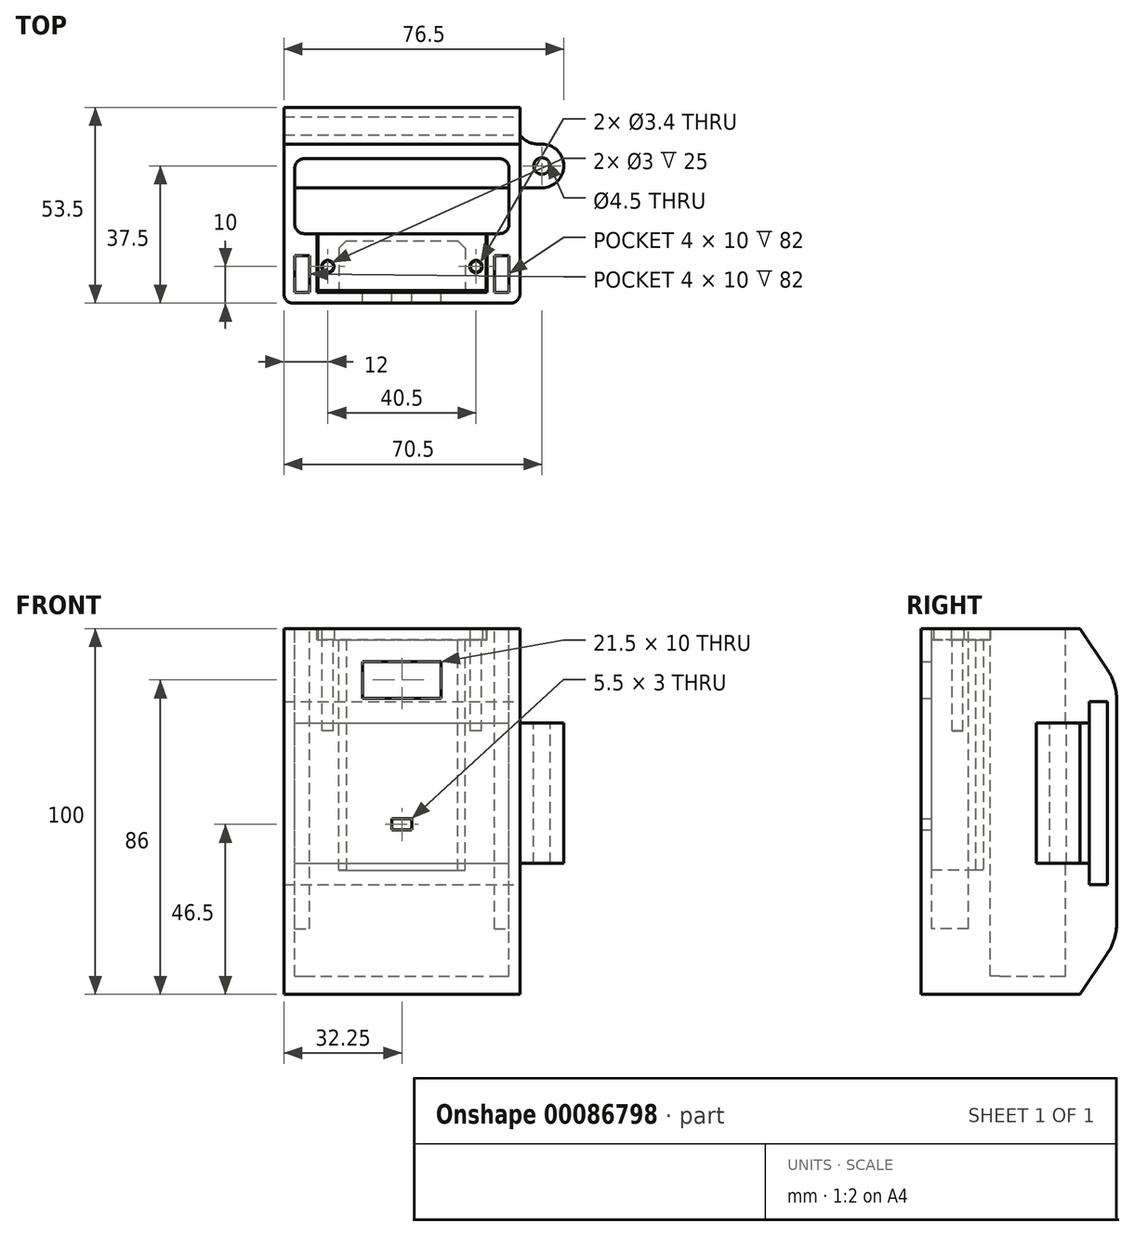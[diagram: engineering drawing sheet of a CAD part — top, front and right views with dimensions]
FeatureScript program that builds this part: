
annotation { "Feature Type Name" : "Feature", "Feature Type Description" : "" }
export const myFeature = defineFeature(function(context is Context, id is Id, definition is map)
    precondition{}
    {
        {
            var Q0;
            Q0=qCreatedBy(makeId("Top.planeOp"),FACE);
            var sketch = newSketch(context, id + "F0", { "sketchPlane" : qUnion([Q0])});
            skLineSegment(sketch, "E0.top", {"start": v(0, 43.5) * mm, "end": v(64.5, 43.5) * mm});
            skLineSegment(sketch, "E0.left", {"start": v(0, 0) * mm, "end": v(0, 43.5) * mm});
            skLineSegment(sketch, "E0.right", {"start": v(64.5, 0) * mm, "end": v(64.5, 43.5) * mm});
            skLineSegment(sketch, "E1.bottom", {"start": v(3, 19) * mm, "end": v(61.5, 19) * mm});
            skLineSegment(sketch, "E1.top", {"start": v(3, 39.5) * mm, "end": v(61.5, 39.5) * mm});
            skLineSegment(sketch, "E1.left", {"start": v(3, 19) * mm, "end": v(3, 39.5) * mm});
            skLineSegment(sketch, "E1.right", {"start": v(61.5, 19) * mm, "end": v(61.5, 39.5) * mm});
            skLineSegment(sketch, "E2.bottom", {"start": v(57.5, 13) * mm, "end": v(61.5, 13) * mm});
            skLineSegment(sketch, "E2.top", {"start": v(57.5, 3) * mm, "end": v(61.5, 3) * mm});
            skLineSegment(sketch, "E2.left", {"start": v(57.5, 13) * mm, "end": v(57.5, 3) * mm});
            skLineSegment(sketch, "E2.right", {"start": v(61.5, 13) * mm, "end": v(61.5, 3) * mm});
            skLineSegment(sketch, "E3", {"start": v(64.5, 43.5) * mm, "end": v(70.5, 43.5) * mm});
            skArc(sketch, "E4", {"start": v(70.5, 31.5) * mm, "mid": v(76.5, 37.5) * mm, "end": v(70.5, 43.5) * mm});
            skLineSegment(sketch, "E5", {"start": v(70.5, 31.5) * mm, "end": v(64.5, 31.5) * mm});
            skLineSegment(sketch, "E6", {"start": v(70.5, 37.5) * mm, "end": v(76.5, 37.5) * mm, "construction": true});
            skCircle(sketch, "E7", {"center": v(70.5, 37.5) * mm, "radius": 2.25 * mm});
            skCircle(sketch, "E8", {"center": v(70.5, 37.5) * mm, "radius": 3.75 * mm});
            skLineSegment(sketch, "E9.bottom", {"start": v(3, 13) * mm, "end": v(7, 13) * mm});
            skLineSegment(sketch, "E9.top", {"start": v(3, 3) * mm, "end": v(7, 3) * mm});
            skLineSegment(sketch, "E9.left", {"start": v(3, 13) * mm, "end": v(3, 3) * mm});
            skLineSegment(sketch, "E9.right", {"start": v(7, 13) * mm, "end": v(7, 3) * mm});
            skLineSegment(sketch, "E10", {"start": v(0, 31.5) * mm, "end": v(-6, 31.5) * mm});
            skArc(sketch, "E11", {"start": v(-6, 43.5) * mm, "mid": v(-12, 37.5) * mm, "end": v(-6, 31.5) * mm});
            skLineSegment(sketch, "E12", {"start": v(-6, 43.5) * mm, "end": v(0, 43.5) * mm});
            skLineSegment(sketch, "E13", {"start": v(-6, 37.5) * mm, "end": v(-12, 37.5) * mm, "construction": true});
            skCircle(sketch, "E14", {"center": v(-6, 37.5) * mm, "radius": 2.25 * mm});
            skCircle(sketch, "E15", {"center": v(-6, 37.5) * mm, "radius": 3.75 * mm});
            skLineSegment(sketch, "E16", {"start": v(64.5, 0) * mm, "end": v(0, 0) * mm});
            skLineSegment(sketch, "E17.bottom", {"start": v(15, 17) * mm, "end": v(49.5, 17) * mm});
            skLineSegment(sketch, "E17.top", {"start": v(15, 3) * mm, "end": v(49.5, 3) * mm});
            skLineSegment(sketch, "E17.left", {"start": v(15, 17) * mm, "end": v(15, 3) * mm});
            skLineSegment(sketch, "E17.right", {"start": v(49.5, 17) * mm, "end": v(49.5, 3) * mm});
            skLineSegment(sketch, "E18", {"start": v(15, 10) * mm, "end": v(0, 10) * mm, "construction": true});
            skLineSegment(sketch, "E19", {"start": v(49.5, 10) * mm, "end": v(64.5, 10) * mm, "construction": true});
            skLineSegment(sketch, "E20", {"start": v(9, 19) * mm, "end": v(9, 3) * mm});
            skLineSegment(sketch, "E21", {"start": v(9, 3) * mm, "end": v(15, 3) * mm});
            skLineSegment(sketch, "E22", {"start": v(49.5, 3) * mm, "end": v(55.5, 3) * mm});
            skLineSegment(sketch, "E23", {"start": v(55.5, 3) * mm, "end": v(55.5, 19) * mm});
            skLineSegment(sketch, "E24", {"start": v(9, 10) * mm, "end": v(15, 10) * mm, "construction": true});
            skLineSegment(sketch, "E25", {"start": v(49.5, 10) * mm, "end": v(55.5, 10) * mm, "construction": true});
            skCircle(sketch, "E26", {"center": v(52.5, 10) * mm, "radius": 1.5 * mm});
            skCircle(sketch, "E27", {"center": v(12, 10) * mm, "radius": 1.5 * mm});
            skSolve(sketch);
        }
        {
            var Q0;
            {var subQ7=sQuery(id+"F0.wireOp",EDGE,"E0.top");Q0=makeQuery(id+"F0.imprint","IMPRINT",FACE,{"disambiguationData":[TD([[makeQuery(id+"F0.imprint","IMPRINT",EDGE,{"derivedFrom":subQ7}),-1.0]])]});}
            extrude(context, id + "F1", {"entities" : qUnion([Q0]), "oppositeDirection" : true, "depth" : 100 * mm});
        }
        {
            var Q0;
            Q0=makeQuery(id+"F0.imprint","IMPRINT",FACE,{"disambiguationData":[TD([[makeQuery(id+"F0.imprint","IMPRINT",EDGE,{"derivedFrom":sQuery(id+"F0.wireOp",EDGE,"E17.bottom")}),1.0]])]});
            var Q1;
            Q1=makeQuery(id+"F1.opExtrude","CAP_FACE",FACE,{"disambiguationData":[OSD([sQuery(id+"F0.wireOp",EDGE,"E0.top"),sQuery(id+"F0.wireOp",EDGE,"E0.left"),sQuery(id+"F0.wireOp",EDGE,"E0.right"),sQuery(id+"F0.wireOp",EDGE,"E1.bottom"),sQuery(id+"F0.wireOp",EDGE,"E1.top"),sQuery(id+"F0.wireOp",EDGE,"E1.left"),sQuery(id+"F0.wireOp",EDGE,"E1.right"),sQuery(id+"F0.wireOp",EDGE,"E2.bottom"),sQuery(id+"F0.wireOp",EDGE,"E2.top"),sQuery(id+"F0.wireOp",EDGE,"E2.left"),sQuery(id+"F0.wireOp",EDGE,"E2.right"),sQuery(id+"F0.wireOp",EDGE,"E9.bottom"),sQuery(id+"F0.wireOp",EDGE,"E9.top"),sQuery(id+"F0.wireOp",EDGE,"E9.left"),sQuery(id+"F0.wireOp",EDGE,"E9.right"),sQuery(id+"F0.wireOp",EDGE,"E16"),sQuery(id+"F0.wireOp",EDGE,"E17.top"),sQuery(id+"F0.wireOp",EDGE,"E20"),sQuery(id+"F0.wireOp",EDGE,"E21"),sQuery(id+"F0.wireOp",EDGE,"E22"),sQuery(id+"F0.wireOp",EDGE,"E23")])],"isStart":false});
            extrude(context, id + "F2", {"entities" : qUnion([Q0]), "operationType" : NewBodyOperationType.ADD, "endBound" : BoundingType.UP_TO_SURFACE, "oppositeDirection" : true, "endBoundEntityFace" : qUnion([Q1]), "depth" : 25 * mm, "hasSecondDirection" : true, "secondDirectionOppositeDirection" : true, "secondDirectionDepth" : 3 * mm});
        }
        {
            var Q0;
            Q0=makeQuery(id+"F0.imprint","IMPRINT",FACE,{"disambiguationData":[TD([[makeQuery(id+"F0.imprint","IMPRINT",EDGE,{"derivedFrom":sQuery(id+"F0.wireOp",EDGE,"E26")}),1.0]])]});
            var Q1;
            Q1=makeQuery(id+"F0.imprint","IMPRINT",FACE,{"disambiguationData":[TD([[makeQuery(id+"F0.imprint","IMPRINT",EDGE,{"derivedFrom":sQuery(id+"F0.wireOp",EDGE,"E27")}),1.0]])]});
            var Q2;
            {var subQ0=sQuery(id+"F0.wireOp",EDGE,"E23");var subQ1=sQuery(id+"F0.wireOp",EDGE,"E22");var subQ2=sQuery(id+"F0.wireOp",EDGE,"E21");var subQ3=sQuery(id+"F0.wireOp",EDGE,"E20");var subQ4=sQuery(id+"F0.wireOp",EDGE,"E17.top");var subQ5=sQuery(id+"F0.wireOp",EDGE,"E16");var subQ6=sQuery(id+"F0.wireOp",EDGE,"E9.right");var subQ7=sQuery(id+"F0.wireOp",EDGE,"E9.left");var subQ8=sQuery(id+"F0.wireOp",EDGE,"E9.top");var subQ9=sQuery(id+"F0.wireOp",EDGE,"E9.bottom");var subQ10=sQuery(id+"F0.wireOp",EDGE,"E2.right");var subQ11=sQuery(id+"F0.wireOp",EDGE,"E2.left");var subQ12=sQuery(id+"F0.wireOp",EDGE,"E2.top");var subQ13=sQuery(id+"F0.wireOp",EDGE,"E2.bottom");var subQ14=sQuery(id+"F0.wireOp",EDGE,"E1.right");var subQ15=sQuery(id+"F0.wireOp",EDGE,"E1.left");var subQ16=sQuery(id+"F0.wireOp",EDGE,"E1.top");var subQ17=sQuery(id+"F0.wireOp",EDGE,"E1.bottom");var subQ18=sQuery(id+"F0.wireOp",EDGE,"E0.right");var subQ19=sQuery(id+"F0.wireOp",EDGE,"E0.left");var subQ20=sQuery(id+"F0.wireOp",EDGE,"E0.top");Q2=makeQuery(id+"F2.boolean.opBoolean","MERGE",FACE,{"derivedFrom":[makeQuery(id+"F1.opExtrude","CAP_FACE",FACE,{"disambiguationData":[OSD([subQ20,subQ19,subQ18,subQ17,subQ16,subQ15,subQ14,subQ13,subQ12,subQ11,subQ10,subQ9,subQ8,subQ7,subQ6,subQ5,subQ4,subQ3,subQ2,subQ1,subQ0])],"isStart":false}),makeQuery(id+"F2.opExtrude","CAP_FACE",FACE,{"disambiguationData":[OSD([subQ20,subQ19,subQ18,subQ17,subQ16,subQ15,subQ14,subQ13,subQ12,subQ11,subQ10,subQ9,subQ8,subQ7,subQ6,subQ5,subQ4,subQ3,subQ2,subQ1,subQ0])],"isStart":false})]});}
            extrude(context, id + "F3", {"entities" : qUnion([Q0, Q1]), "operationType" : NewBodyOperationType.ADD, "endBound" : BoundingType.UP_TO_SURFACE, "oppositeDirection" : true, "endBoundEntityFace" : qUnion([Q2]), "depth" : 25 * mm, "hasSecondDirection" : true, "secondDirectionOppositeDirection" : true, "secondDirectionDepth" : 28 * mm});
        }
        {
            var Q0;
            Q0=makeQuery(id+"F0.imprint","IMPRINT",FACE,{"disambiguationData":[TD([[makeQuery(id+"F0.imprint","IMPRINT",EDGE,{"derivedFrom":sQuery(id+"F0.wireOp",EDGE,"E1.top")}),-1.0]])]});
            var Q1;
            {var subQ0=sQuery(id+"F0.wireOp",EDGE,"E23");var subQ1=sQuery(id+"F0.wireOp",EDGE,"E22");var subQ2=sQuery(id+"F0.wireOp",EDGE,"E21");var subQ3=sQuery(id+"F0.wireOp",EDGE,"E20");var subQ4=sQuery(id+"F0.wireOp",EDGE,"E17.top");var subQ5=sQuery(id+"F0.wireOp",EDGE,"E16");var subQ6=sQuery(id+"F0.wireOp",EDGE,"E9.right");var subQ7=sQuery(id+"F0.wireOp",EDGE,"E9.left");var subQ8=sQuery(id+"F0.wireOp",EDGE,"E9.top");var subQ9=sQuery(id+"F0.wireOp",EDGE,"E9.bottom");var subQ10=sQuery(id+"F0.wireOp",EDGE,"E2.right");var subQ11=sQuery(id+"F0.wireOp",EDGE,"E2.left");var subQ12=sQuery(id+"F0.wireOp",EDGE,"E2.top");var subQ13=sQuery(id+"F0.wireOp",EDGE,"E2.bottom");var subQ14=sQuery(id+"F0.wireOp",EDGE,"E1.right");var subQ15=sQuery(id+"F0.wireOp",EDGE,"E1.left");var subQ16=sQuery(id+"F0.wireOp",EDGE,"E1.top");var subQ17=sQuery(id+"F0.wireOp",EDGE,"E1.bottom");var subQ18=sQuery(id+"F0.wireOp",EDGE,"E0.right");var subQ19=sQuery(id+"F0.wireOp",EDGE,"E0.left");var subQ20=sQuery(id+"F0.wireOp",EDGE,"E0.top");Q1=makeQuery(id+"F3.boolean.opBoolean","MERGE",FACE,{"derivedFrom":[makeQuery(id+"F2.boolean.opBoolean","MERGE",FACE,{"derivedFrom":[makeQuery(id+"F1.opExtrude","CAP_FACE",FACE,{"disambiguationData":[OSD([subQ20,subQ19,subQ18,subQ17,subQ16,subQ15,subQ14,subQ13,subQ12,subQ11,subQ10,subQ9,subQ8,subQ7,subQ6,subQ5,subQ4,subQ3,subQ2,subQ1,subQ0])],"isStart":false}),makeQuery(id+"F2.opExtrude","CAP_FACE",FACE,{"disambiguationData":[OSD([subQ20,subQ19,subQ18,subQ17,subQ16,subQ15,subQ14,subQ13,subQ12,subQ11,subQ10,subQ9,subQ8,subQ7,subQ6,subQ5,subQ4,subQ3,subQ2,subQ1,subQ0])],"isStart":false})]}),makeQuery(id+"F3.opExtrude","CAP_FACE",FACE,{"disambiguationData":[OSD([subQ20,subQ19,subQ18,subQ17,subQ16,subQ15,subQ14,subQ13,subQ12,subQ11,subQ10,subQ9,subQ8,subQ7,subQ6,subQ5,subQ4,subQ3,subQ2,subQ1,subQ0]),ownerDisambiguation([makeQuery(id+"F3.opExtrude","SWEPT_BODY",BODY,{"disambiguationData":[OSD([sQuery(id+"F0.wireOp",EDGE,"E26")])]})])],"isStart":false}),makeQuery(id+"F3.opExtrude","CAP_FACE",FACE,{"disambiguationData":[OSD([subQ20,subQ19,subQ18,subQ17,subQ16,subQ15,subQ14,subQ13,subQ12,subQ11,subQ10,subQ9,subQ8,subQ7,subQ6,subQ5,subQ4,subQ3,subQ2,subQ1,subQ0]),ownerDisambiguation([makeQuery(id+"F3.opExtrude","SWEPT_BODY",BODY,{"disambiguationData":[OSD([sQuery(id+"F0.wireOp",EDGE,"E27")])]})])],"isStart":false})]});}
            extrude(context, id + "F4", {"entities" : qUnion([Q0]), "operationType" : NewBodyOperationType.ADD, "endBound" : BoundingType.UP_TO_SURFACE, "oppositeDirection" : true, "endBoundEntityFace" : qUnion([Q1]), "depth" : 25 * mm, "hasSecondDirection" : true, "secondDirectionOppositeDirection" : true, "secondDirectionDepth" : 95 * mm});
        }
        {
            var Q0;
            Q0=makeQuery(id+"F0.imprint","IMPRINT",FACE,{"disambiguationData":[TD([[makeQuery(id+"F0.imprint","IMPRINT",EDGE,{"derivedFrom":sQuery(id+"F0.wireOp",EDGE,"E17.bottom")}),-1.0]])]});
            var Q1;
            {var subQ0=sQuery(id+"F0.wireOp",EDGE,"E23");var subQ1=sQuery(id+"F0.wireOp",EDGE,"E22");var subQ2=sQuery(id+"F0.wireOp",EDGE,"E21");var subQ3=sQuery(id+"F0.wireOp",EDGE,"E20");var subQ4=sQuery(id+"F0.wireOp",EDGE,"E17.top");var subQ5=sQuery(id+"F0.wireOp",EDGE,"E16");var subQ6=sQuery(id+"F0.wireOp",EDGE,"E9.right");var subQ7=sQuery(id+"F0.wireOp",EDGE,"E9.left");var subQ8=sQuery(id+"F0.wireOp",EDGE,"E9.top");var subQ9=sQuery(id+"F0.wireOp",EDGE,"E9.bottom");var subQ10=sQuery(id+"F0.wireOp",EDGE,"E2.right");var subQ11=sQuery(id+"F0.wireOp",EDGE,"E2.left");var subQ12=sQuery(id+"F0.wireOp",EDGE,"E2.top");var subQ13=sQuery(id+"F0.wireOp",EDGE,"E2.bottom");var subQ14=sQuery(id+"F0.wireOp",EDGE,"E1.right");var subQ15=sQuery(id+"F0.wireOp",EDGE,"E1.left");var subQ16=sQuery(id+"F0.wireOp",EDGE,"E1.top");var subQ17=sQuery(id+"F0.wireOp",EDGE,"E1.bottom");var subQ18=sQuery(id+"F0.wireOp",EDGE,"E0.right");var subQ19=sQuery(id+"F0.wireOp",EDGE,"E0.left");var subQ20=sQuery(id+"F0.wireOp",EDGE,"E0.top");Q1=makeQuery(id+"F4.boolean.opBoolean","MERGE",FACE,{"derivedFrom":[makeQuery(id+"F3.boolean.opBoolean","MERGE",FACE,{"derivedFrom":[makeQuery(id+"F2.boolean.opBoolean","MERGE",FACE,{"derivedFrom":[makeQuery(id+"F1.opExtrude","CAP_FACE",FACE,{"disambiguationData":[OSD([subQ20,subQ19,subQ18,subQ17,subQ16,subQ15,subQ14,subQ13,subQ12,subQ11,subQ10,subQ9,subQ8,subQ7,subQ6,subQ5,subQ4,subQ3,subQ2,subQ1,subQ0])],"isStart":false}),makeQuery(id+"F2.opExtrude","CAP_FACE",FACE,{"disambiguationData":[OSD([subQ20,subQ19,subQ18,subQ17,subQ16,subQ15,subQ14,subQ13,subQ12,subQ11,subQ10,subQ9,subQ8,subQ7,subQ6,subQ5,subQ4,subQ3,subQ2,subQ1,subQ0])],"isStart":false})]}),makeQuery(id+"F3.opExtrude","CAP_FACE",FACE,{"disambiguationData":[OSD([subQ20,subQ19,subQ18,subQ17,subQ16,subQ15,subQ14,subQ13,subQ12,subQ11,subQ10,subQ9,subQ8,subQ7,subQ6,subQ5,subQ4,subQ3,subQ2,subQ1,subQ0]),ownerDisambiguation([makeQuery(id+"F3.opExtrude","SWEPT_BODY",BODY,{"disambiguationData":[OSD([sQuery(id+"F0.wireOp",EDGE,"E26")])]})])],"isStart":false}),makeQuery(id+"F3.opExtrude","CAP_FACE",FACE,{"disambiguationData":[OSD([subQ20,subQ19,subQ18,subQ17,subQ16,subQ15,subQ14,subQ13,subQ12,subQ11,subQ10,subQ9,subQ8,subQ7,subQ6,subQ5,subQ4,subQ3,subQ2,subQ1,subQ0]),ownerDisambiguation([makeQuery(id+"F3.opExtrude","SWEPT_BODY",BODY,{"disambiguationData":[OSD([sQuery(id+"F0.wireOp",EDGE,"E27")])]})])],"isStart":false})]}),makeQuery(id+"F4.opExtrude","CAP_FACE",FACE,{"disambiguationData":[OSD([subQ20,subQ19,subQ18,subQ17,subQ16,subQ15,subQ14,subQ13,subQ12,subQ11,subQ10,subQ9,subQ8,subQ7,subQ6,subQ5,subQ4,subQ3,subQ2,subQ1,subQ0])],"isStart":false})]});}
            extrude(context, id + "F5", {"entities" : qUnion([Q0]), "operationType" : NewBodyOperationType.ADD, "endBound" : BoundingType.UP_TO_SURFACE, "oppositeDirection" : true, "endBoundEntityFace" : qUnion([Q1]), "depth" : 25 * mm, "hasSecondDirection" : true, "secondDirectionOppositeDirection" : true, "secondDirectionDepth" : 66 * mm});
        }
        {
            var Q0;
            {var subQ1=sQuery(id+"F0.wireOp",EDGE,"E3");Q0=makeQuery(id+"F0.imprint","IMPRINT",FACE,{"disambiguationData":[TD([[makeQuery(id+"F0.imprint","IMPRINT",EDGE,{"derivedFrom":subQ1}),-1.0]])]});}
            var Q1;
            Q1=makeQuery(id+"F0.imprint","IMPRINT",FACE,{"disambiguationData":[TD([[makeQuery(id+"F0.imprint","IMPRINT",EDGE,{"derivedFrom":sQuery(id+"F0.wireOp",EDGE,"E7")}),-1.0]])]});
            extrude(context, id + "F6", {"entities" : qUnion([Q0, Q1]), "operationType" : NewBodyOperationType.ADD, "oppositeDirection" : true, "depth" : 64.2 * mm, "hasSecondDirection" : true, "secondDirectionOppositeDirection" : true, "secondDirectionDepth" : 25.8 * mm});
        }
        {
            var Q0;
            Q0=makeQuery(id+"F0.imprint","IMPRINT",FACE,{"disambiguationData":[TD([[makeQuery(id+"F0.imprint","IMPRINT",EDGE,{"derivedFrom":sQuery(id+"F0.wireOp",EDGE,"E9.bottom")}),-1.0]])]});
            var Q1;
            Q1=makeQuery(id+"F0.imprint","IMPRINT",FACE,{"disambiguationData":[TD([[makeQuery(id+"F0.imprint","IMPRINT",EDGE,{"derivedFrom":sQuery(id+"F0.wireOp",EDGE,"E2.bottom")}),-1.0]])]});
            var Q2;
            {var subQ0=sQuery(id+"F0.wireOp",EDGE,"E23");var subQ1=sQuery(id+"F0.wireOp",EDGE,"E22");var subQ2=sQuery(id+"F0.wireOp",EDGE,"E21");var subQ3=sQuery(id+"F0.wireOp",EDGE,"E20");var subQ4=sQuery(id+"F0.wireOp",EDGE,"E17.top");var subQ5=sQuery(id+"F0.wireOp",EDGE,"E16");var subQ6=sQuery(id+"F0.wireOp",EDGE,"E9.right");var subQ7=sQuery(id+"F0.wireOp",EDGE,"E9.left");var subQ8=sQuery(id+"F0.wireOp",EDGE,"E9.top");var subQ9=sQuery(id+"F0.wireOp",EDGE,"E9.bottom");var subQ10=sQuery(id+"F0.wireOp",EDGE,"E2.right");var subQ11=sQuery(id+"F0.wireOp",EDGE,"E2.left");var subQ12=sQuery(id+"F0.wireOp",EDGE,"E2.top");var subQ13=sQuery(id+"F0.wireOp",EDGE,"E2.bottom");var subQ14=sQuery(id+"F0.wireOp",EDGE,"E1.right");var subQ15=sQuery(id+"F0.wireOp",EDGE,"E1.left");var subQ16=sQuery(id+"F0.wireOp",EDGE,"E1.top");var subQ17=sQuery(id+"F0.wireOp",EDGE,"E1.bottom");var subQ18=sQuery(id+"F0.wireOp",EDGE,"E0.right");var subQ19=sQuery(id+"F0.wireOp",EDGE,"E0.left");var subQ20=sQuery(id+"F0.wireOp",EDGE,"E0.top");Q2=makeQuery(id+"F5.boolean.opBoolean","MERGE",FACE,{"derivedFrom":[makeQuery(id+"F4.boolean.opBoolean","MERGE",FACE,{"derivedFrom":[makeQuery(id+"F3.boolean.opBoolean","MERGE",FACE,{"derivedFrom":[makeQuery(id+"F2.boolean.opBoolean","MERGE",FACE,{"derivedFrom":[makeQuery(id+"F1.opExtrude","CAP_FACE",FACE,{"disambiguationData":[OSD([subQ20,subQ19,subQ18,subQ17,subQ16,subQ15,subQ14,subQ13,subQ12,subQ11,subQ10,subQ9,subQ8,subQ7,subQ6,subQ5,subQ4,subQ3,subQ2,subQ1,subQ0])],"isStart":false}),makeQuery(id+"F2.opExtrude","CAP_FACE",FACE,{"disambiguationData":[OSD([subQ20,subQ19,subQ18,subQ17,subQ16,subQ15,subQ14,subQ13,subQ12,subQ11,subQ10,subQ9,subQ8,subQ7,subQ6,subQ5,subQ4,subQ3,subQ2,subQ1,subQ0])],"isStart":false})]}),makeQuery(id+"F3.opExtrude","CAP_FACE",FACE,{"disambiguationData":[OSD([subQ20,subQ19,subQ18,subQ17,subQ16,subQ15,subQ14,subQ13,subQ12,subQ11,subQ10,subQ9,subQ8,subQ7,subQ6,subQ5,subQ4,subQ3,subQ2,subQ1,subQ0]),ownerDisambiguation([makeQuery(id+"F3.opExtrude","SWEPT_BODY",BODY,{"disambiguationData":[OSD([sQuery(id+"F0.wireOp",EDGE,"E26")])]})])],"isStart":false}),makeQuery(id+"F3.opExtrude","CAP_FACE",FACE,{"disambiguationData":[OSD([subQ20,subQ19,subQ18,subQ17,subQ16,subQ15,subQ14,subQ13,subQ12,subQ11,subQ10,subQ9,subQ8,subQ7,subQ6,subQ5,subQ4,subQ3,subQ2,subQ1,subQ0]),ownerDisambiguation([makeQuery(id+"F3.opExtrude","SWEPT_BODY",BODY,{"disambiguationData":[OSD([sQuery(id+"F0.wireOp",EDGE,"E27")])]})])],"isStart":false})]}),makeQuery(id+"F4.opExtrude","CAP_FACE",FACE,{"disambiguationData":[OSD([subQ20,subQ19,subQ18,subQ17,subQ16,subQ15,subQ14,subQ13,subQ12,subQ11,subQ10,subQ9,subQ8,subQ7,subQ6,subQ5,subQ4,subQ3,subQ2,subQ1,subQ0])],"isStart":false})]}),makeQuery(id+"F5.opExtrude","CAP_FACE",FACE,{"disambiguationData":[OSD([subQ20,subQ19,subQ18,subQ17,subQ16,subQ15,subQ14,subQ13,subQ12,subQ11,subQ10,subQ9,subQ8,subQ7,subQ6,subQ5,subQ4,subQ3,subQ2,subQ1,subQ0])],"isStart":false})]});}
            extrude(context, id + "F7", {"entities" : qUnion([Q0, Q1]), "operationType" : NewBodyOperationType.ADD, "endBound" : BoundingType.UP_TO_SURFACE, "oppositeDirection" : true, "endBoundEntityFace" : qUnion([Q2]), "depth" : 25 * mm, "hasSecondDirection" : true, "secondDirectionOppositeDirection" : true, "secondDirectionDepth" : 82 * mm});
        }
        {
            var Q0;
            Q0=makeQuery(id+"F1.opExtrude","SWEPT_FACE",FACE,{"disambiguationData":[OSD([sQuery(id+"F0.wireOp",EDGE,"E0.right")])]});
            var sketch = newSketch(context, id + "F8", { "sketchPlane" : qUnion([Q0])});
            skLineSegment(sketch, "E28", {"start": v(43.5, 0) * mm, "end": v(53.5, -15) * mm});
            skLineSegment(sketch, "E29", {"start": v(53.5, -15) * mm, "end": v(53.5, -85) * mm});
            skLineSegment(sketch, "E30", {"start": v(53.5, -85) * mm, "end": v(43.5, -100) * mm});
            skLineSegment(sketch, "E31.bottom", {"start": v(46, -20) * mm, "end": v(51, -20) * mm});
            skLineSegment(sketch, "E31.top", {"start": v(46, -70) * mm, "end": v(51, -70) * mm});
            skLineSegment(sketch, "E31.left", {"start": v(46, -20) * mm, "end": v(46, -70) * mm});
            skLineSegment(sketch, "E31.right", {"start": v(51, -20) * mm, "end": v(51, -70) * mm});
            skLineSegment(sketch, "E32", {"start": v(53.5, -15) * mm, "end": v(43.5, -15) * mm, "construction": true});
            skSolve(sketch);
        }
        {
            var Q0;
            Q0=makeQuery(id+"F8.imprint","IMPRINT",FACE,{"disambiguationData":[TD([[makeQuery(id+"F8.imprint","IMPRINT",EDGE,{"derivedFrom":sQuery(id+"F8.wireOp",EDGE,"E28")}),-1.0]])]});
            var Q1;
            Q1=makeQuery(id+"F1.opExtrude","SWEPT_FACE",FACE,{"disambiguationData":[OSD([sQuery(id+"F0.wireOp",EDGE,"E0.left")])]});
            extrude(context, id + "F9", {"entities" : qUnion([Q0]), "operationType" : NewBodyOperationType.ADD, "endBound" : BoundingType.UP_TO_SURFACE, "oppositeDirection" : true, "endBoundEntityFace" : qUnion([Q1]), "depth" : 25 * mm});
        }
        {
            var Q0;
            Q0=makeQuery(id+"F2.opExtrude","CAP_FACE",FACE,{"disambiguationData":[OSD([sQuery(id+"F0.wireOp",EDGE,"E1.bottom"),sQuery(id+"F0.wireOp",EDGE,"E17.bottom"),sQuery(id+"F0.wireOp",EDGE,"E17.left"),sQuery(id+"F0.wireOp",EDGE,"E17.right"),sQuery(id+"F0.wireOp",EDGE,"E20"),sQuery(id+"F0.wireOp",EDGE,"E21"),sQuery(id+"F0.wireOp",EDGE,"E22"),sQuery(id+"F0.wireOp",EDGE,"E23"),sQuery(id+"F0.wireOp",EDGE,"E26"),sQuery(id+"F0.wireOp",EDGE,"E27")])],"isStart":true});
            var sketch = newSketch(context, id + "F10", { "sketchPlane" : qUnion([Q0])});
            skLineSegment(sketch, "E33", {"start": v(9.25, 3.5) * mm, "end": v(9.25, 19) * mm});
            skLineSegment(sketch, "E34", {"start": v(9.25, 19) * mm, "end": v(55.25, 19) * mm});
            skLineSegment(sketch, "E35", {"start": v(55.25, 19) * mm, "end": v(55.25, 3.5) * mm});
            skLineSegment(sketch, "E36", {"start": v(55.25, 3.5) * mm, "end": v(9.25, 3.5) * mm});
            skCircle(sketch, "E37", {"center": v(12, 10) * mm, "radius": 1.7 * mm});
            skCircle(sketch, "E38", {"center": v(52.5, 10) * mm, "radius": 1.7 * mm});
            skSolve(sketch);
        }
        {
            var Q0;
            Q0 = qSketchRegion(id + "F10", true);
            var Q1;
            Q1=makeQuery(id+"F1.opExtrude","CAP_FACE",FACE,{"disambiguationData":[OSD([sQuery(id+"F0.wireOp",EDGE,"E0.top"),sQuery(id+"F0.wireOp",EDGE,"E0.left"),sQuery(id+"F0.wireOp",EDGE,"E0.right"),sQuery(id+"F0.wireOp",EDGE,"E1.bottom"),sQuery(id+"F0.wireOp",EDGE,"E1.top"),sQuery(id+"F0.wireOp",EDGE,"E1.left"),sQuery(id+"F0.wireOp",EDGE,"E1.right"),sQuery(id+"F0.wireOp",EDGE,"E2.bottom"),sQuery(id+"F0.wireOp",EDGE,"E2.top"),sQuery(id+"F0.wireOp",EDGE,"E2.left"),sQuery(id+"F0.wireOp",EDGE,"E2.right"),sQuery(id+"F0.wireOp",EDGE,"E9.bottom"),sQuery(id+"F0.wireOp",EDGE,"E9.top"),sQuery(id+"F0.wireOp",EDGE,"E9.left"),sQuery(id+"F0.wireOp",EDGE,"E9.right"),sQuery(id+"F0.wireOp",EDGE,"E16"),sQuery(id+"F0.wireOp",EDGE,"E17.top"),sQuery(id+"F0.wireOp",EDGE,"E20"),sQuery(id+"F0.wireOp",EDGE,"E21"),sQuery(id+"F0.wireOp",EDGE,"E22"),sQuery(id+"F0.wireOp",EDGE,"E23")])],"isStart":true});
            extrude(context, id + "F11", {"entities" : qUnion([Q0]), "endBound" : BoundingType.UP_TO_SURFACE, "endBoundEntityFace" : qUnion([Q1]), "depth" : 3 * mm});
        }
        {
            var Q0;
            Q0=makeQuery(id+"F1.opExtrude","SWEPT_FACE",FACE,{"disambiguationData":[OSD([sQuery(id+"F0.wireOp",EDGE,"E17.top"),sQuery(id+"F0.wireOp",EDGE,"E21"),sQuery(id+"F0.wireOp",EDGE,"E22")])]});
            var sketch = newSketch(context, id + "F12", { "sketchPlane" : qUnion([Q0])});
            skLineSegment(sketch, "E39.bottom", {"start": v(-21.5, -19) * mm, "end": v(-43, -19) * mm});
            skLineSegment(sketch, "E39.top", {"start": v(-21.5, -9) * mm, "end": v(-43, -9) * mm});
            skLineSegment(sketch, "E39.left", {"start": v(-21.5, -19) * mm, "end": v(-21.5, -9) * mm});
            skLineSegment(sketch, "E39.right", {"start": v(-43, -19) * mm, "end": v(-43, -9) * mm});
            skLineSegment(sketch, "E40", {"start": v(-15, -3) * mm, "end": v(-49.5, -3) * mm, "construction": true});
            skLineSegment(sketch, "E41.bottom", {"start": v(-29.5, -55) * mm, "end": v(-35, -55) * mm});
            skLineSegment(sketch, "E41.top", {"start": v(-29.5, -52) * mm, "end": v(-35, -52) * mm});
            skLineSegment(sketch, "E41.left", {"start": v(-29.5, -55) * mm, "end": v(-29.5, -52) * mm});
            skLineSegment(sketch, "E41.right", {"start": v(-35, -55) * mm, "end": v(-35, -52) * mm});
            skLineSegment(sketch, "E42", {"start": v(-29.5, -53.5) * mm, "end": v(-15, -53.5) * mm, "construction": true});
            skLineSegment(sketch, "E43", {"start": v(-35, -53.5) * mm, "end": v(-49.5, -53.5) * mm, "construction": true});
            skSolve(sketch);
        }
        {
            var Q0;
            Q0=makeQuery(id+"F12.imprint","IMPRINT",FACE,{"disambiguationData":[TD([[makeQuery(id+"F12.imprint","IMPRINT",EDGE,{"derivedFrom":sQuery(id+"F12.wireOp",EDGE,"E39.bottom")}),-1.0]])]});
            var Q1;
            Q1=makeQuery(id+"F12.imprint","IMPRINT",FACE,{"disambiguationData":[TD([[makeQuery(id+"F12.imprint","IMPRINT",EDGE,{"derivedFrom":sQuery(id+"F12.wireOp",EDGE,"E41.bottom")}),-1.0]])]});
            var Q2;
            Q2=makeQuery(id+"F1.opExtrude","SWEPT_FACE",FACE,{"disambiguationData":[OSD([sQuery(id+"F0.wireOp",EDGE,"E16")])]});
            extrude(context, id + "F13", {"entities" : qUnion([Q0, Q1]), "operationType" : NewBodyOperationType.REMOVE, "endBound" : BoundingType.UP_TO_SURFACE, "oppositeDirection" : true, "endBoundEntityFace" : qUnion([Q2]), "depth" : 25 * mm});
        }
        {
            var Q0;
            Q0=makeQuery(id+"F1.opExtrude","SWEPT_EDGE",EDGE,{"disambiguationData":[OSD([sQuery(id+"F0.wireOp",EDGE,"E1.top"),sQuery(id+"F0.wireOp",EDGE,"E1.left")])]});
            var Q1;
            Q1=makeQuery(id+"F1.opExtrude","SWEPT_EDGE",EDGE,{"disambiguationData":[OSD([sQuery(id+"F0.wireOp",EDGE,"E1.top"),sQuery(id+"F0.wireOp",EDGE,"E1.right")])]});
            var Q2;
            Q2=makeQuery(id+"F1.opExtrude","SWEPT_EDGE",EDGE,{"disambiguationData":[OSD([sQuery(id+"F0.wireOp",EDGE,"E1.bottom"),sQuery(id+"F0.wireOp",EDGE,"E1.right")])]});
            var Q3;
            Q3=makeQuery(id+"F1.opExtrude","SWEPT_EDGE",EDGE,{"disambiguationData":[OSD([sQuery(id+"F0.wireOp",EDGE,"E1.bottom"),sQuery(id+"F0.wireOp",EDGE,"E1.left")])]});
            fillet(context, id + "F14", {"entities" : qUnion([Q0, Q1, Q2, Q3]), "radius" : 2.5 * mm, "tangentPropagation" : true, "allowEdgeOverflow" : false});
        }
        {
            var Q0;
            Q0=makeQuery(id+"F1.opExtrude","SWEPT_EDGE",EDGE,{"disambiguationData":[OSD([sQuery(id+"F0.wireOp",EDGE,"E0.left"),sQuery(id+"F0.wireOp",EDGE,"E16")])]});
            var Q1;
            Q1=makeQuery(id+"F1.opExtrude","SWEPT_EDGE",EDGE,{"disambiguationData":[OSD([sQuery(id+"F0.wireOp",EDGE,"E0.right"),sQuery(id+"F0.wireOp",EDGE,"E16")])]});
            fillet(context, id + "F15", {"entities" : qUnion([Q0, Q1]), "radius" : 2.5 * mm, "tangentPropagation" : true, "allowEdgeOverflow" : false});
        }
        {
            var Q0;
            Q0=makeQuery(id+"F6.opExtrude","SWEPT_EDGE",EDGE,{"disambiguationData":[OSD([sQuery(id+"F0.wireOp",EDGE,"E0.right"),sQuery(id+"F0.wireOp",EDGE,"E5")])]});
            var Q1;
            {var subQ0=sQuery(id+"F0.wireOp",EDGE,"E3");var subQ1=sQuery(id+"F0.wireOp",EDGE,"E0.top");Q1=makeQuery(id+"F9.boolean.opBoolean","INTERSECT",EDGE,{"derivedFrom":[makeQuery(id+"F6.boolean.opBoolean","MERGE",FACE,{"derivedFrom":[makeQuery(id+"F1.opExtrude","SWEPT_FACE",FACE,{"disambiguationData":[OSD([subQ1])]}),makeQuery(id+"F6.opExtrude","SWEPT_FACE",FACE,{"disambiguationData":[OSD([subQ0])]})]}),makeQuery(id+"F9.opExtrude","CAP_FACE",FACE,{"disambiguationData":[OSD([subQ1,sQuery(id+"F0.wireOp",EDGE,"E0.right"),subQ0,sQuery(id+"F0.wireOp",EDGE,"E5"),sQuery(id+"F8.wireOp",EDGE,"E28"),sQuery(id+"F8.wireOp",EDGE,"E29"),sQuery(id+"F8.wireOp",EDGE,"E30"),sQuery(id+"F8.wireOp",EDGE,"E31.bottom"),sQuery(id+"F8.wireOp",EDGE,"E31.top"),sQuery(id+"F8.wireOp",EDGE,"E31.left"),sQuery(id+"F8.wireOp",EDGE,"E31.right")])],"isStart":true})]});}
            fillet(context, id + "F16", {"entities" : qUnion([Q0, Q1]), "radius" : 6 * mm, "tangentPropagation" : true, "allowEdgeOverflow" : false});
        }
        {
            var Q0;
            Q0=makeQuery(id+"F9.opExtrude","SWEPT_EDGE",EDGE,{"disambiguationData":[OSD([sQuery(id+"F8.wireOp",EDGE,"E28"),sQuery(id+"F8.wireOp",EDGE,"E29")])]});
            var Q1;
            Q1=makeQuery(id+"F9.opExtrude","SWEPT_EDGE",EDGE,{"disambiguationData":[OSD([sQuery(id+"F8.wireOp",EDGE,"E29"),sQuery(id+"F8.wireOp",EDGE,"E30")])]});
            fillet(context, id + "F17", {"entities" : qUnion([Q0, Q1]), "radius" : 15 * mm, "tangentPropagation" : true, "allowEdgeOverflow" : false});
        }
        {
            var Q0;
            Q0=makeQuery(id+"F2.opExtrude","SWEPT_EDGE",EDGE,{"disambiguationData":[OSD([sQuery(id+"F0.wireOp",EDGE,"E17.bottom"),sQuery(id+"F0.wireOp",EDGE,"E17.left")])]});
            var Q1;
            Q1=makeQuery(id+"F2.opExtrude","SWEPT_EDGE",EDGE,{"disambiguationData":[OSD([sQuery(id+"F0.wireOp",EDGE,"E17.bottom"),sQuery(id+"F0.wireOp",EDGE,"E17.right")])]});
            chamfer(context, id + "F18", {"entities" : qUnion([Q0, Q1]), "width" : 2 * mm, "tangentPropagation" : true});
        }
    });
